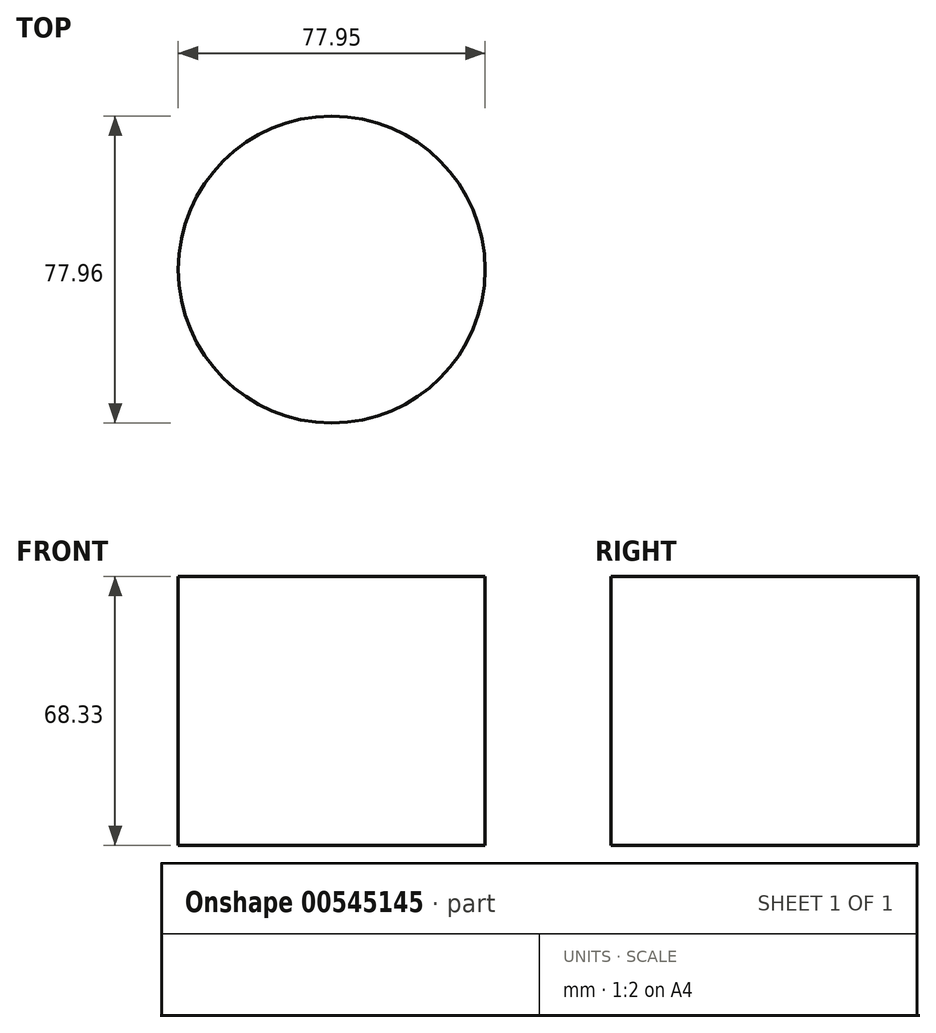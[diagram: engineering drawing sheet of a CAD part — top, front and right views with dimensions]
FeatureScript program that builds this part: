
annotation { "Feature Type Name" : "Feature", "Feature Type Description" : "" }
export const myFeature = defineFeature(function(context is Context, id is Id, definition is map)
    precondition{}
    {
        {
            var Q0;
            Q0=qCreatedBy(makeId("Top.planeOp"),FACE);
            var sketch = newSketch(context, id + "F0", { "sketchPlane" : qUnion([Q0])});
            skCircle(sketch, "E0", {"center": v(-32.33, 0) * mm, "radius": 38.98 * mm});
            skSolve(sketch);
        }
        {
            var Q0;
            Q0=makeQuery(id+"F0.imprint","IMPRINT",FACE,{"disambiguationData":[TD([[makeQuery(id+"F0.imprint","IMPRINT",EDGE,{"derivedFrom":sQuery(id+"F0.wireOp",EDGE,"E0")}),1.0]])]});
            extrude(context, id + "F1", {"entities" : qUnion([Q0]), "depth" : 68.33 * mm, "offsetDistance" : 25.4 * mm});
        }
    });
